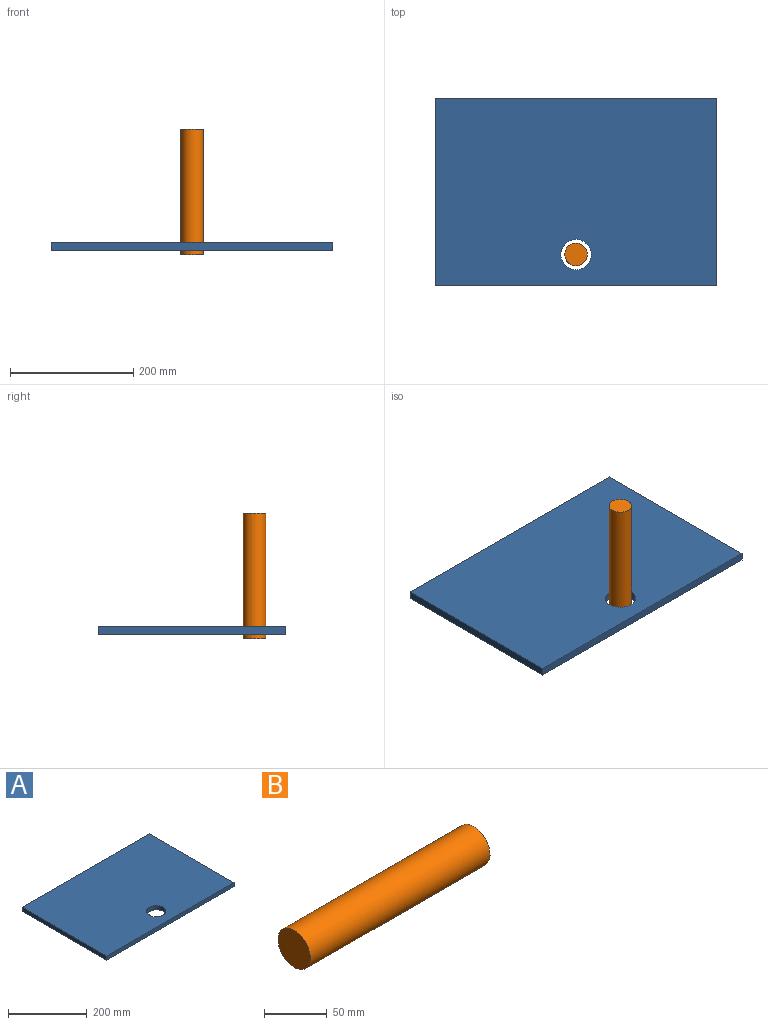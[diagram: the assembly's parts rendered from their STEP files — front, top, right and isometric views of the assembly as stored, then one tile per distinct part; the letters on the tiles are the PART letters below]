
ASSEMBLY  parts=2 mates=1
PART A: 7 faces, bbox 457.2x304.8x12.7 mm
  f0: plane 304.8x12.7mm, normal (1,0,0), area 3871mm2, adj f1,f3,f4,f5
  f1: plane 457.2x12.7mm, normal (0,1,0), area 5806.4mm2, adj f0,f2,f4,f5
  f2: plane 304.8x12.7mm, normal (-1,0,0), area 3871mm2, adj f1,f3,f4,f5
  f3: plane 457.2x12.7mm, normal (0,-1,0), area 5806.4mm2, adj f0,f2,f4,f5
  f4: plane 457.2x304.8mm, normal (0,0,1), area 137452.4mm2, adj f0,f1,f2,f3,f6
  f5: plane 457.2x304.8mm, normal (0,0,-1), area 137452.4mm2, adj f0,f1,f2,f3,f6
  f6: cylinder r=24.61mm len=49.21mm, axis (0,0,1), area 1963.5mm2, adj f4,f5
PART B: 3 faces, bbox 203.2x36.5x36.5 mm
  f0: plane 36.51x36.51mm, normal (-1,0,0), area 1047.1mm2, adj f2
  f1: plane 36.51x36.51mm, normal (1,0,0), area 1047.1mm2, adj f2
  f2: cylinder r=18.26mm len=203.2mm, axis (-1,0,0), area 23308.5mm2, adj f0,f1
PLACE A t=(0,-1.41,-6.35)mm
PLACE B rot(axis=(0,-1,0),90deg) t=(0,-103.01,82.55)mm
MATE fastened B.f2 <-> A.f6  axis (0,0,-1) through (0,-103.01,-19.05)mm
